# Revit family: FU_Chair_Sandler_Mare 1-0_UPH
name_source: partatom
category: Furniture
units: mm (PartAtom-declared; Revit-internal decimal feet)

## family parameters
Always vertical = Yes
Cut with Voids When Loaded = No
OmniClass Number = 23.40.20.00
OmniClass Title = General Furniture and Specialties
Room Calculation Point = No
Shared = No
Work Plane-Based = No

## types (1)
- Mare 1.0 UPH
    Back = Polypropylene - Pistachio - NCS S3010-G50Y
    Default Elevation = 0 mm  [stored 0 ft]
    Depth = 560 mm  [stored 1.83727 ft]
    Description = Aluminum or steel frame arm chair with upholstered seat and polypropylene back. Indoor use only.
    Frame = Metal - Paint -AL VR - Pure White
    Height = 730 mm  [stored 2.39501 ft]
    Manufacturer = Sandler
    Model = Mare 1.0 UPH
    Seat = Fabric - X2 - Algebra AK005
    URL = https://www.sandlerseating.com
    Width = 550 mm

note: [stored X ft] marks values corroborated as IEEE doubles in the binary element streams (Revit-internal decimal feet)

## geometry (parser evidence)
native form markers: Sweep x3
no freeform markers — native parametric forms only
